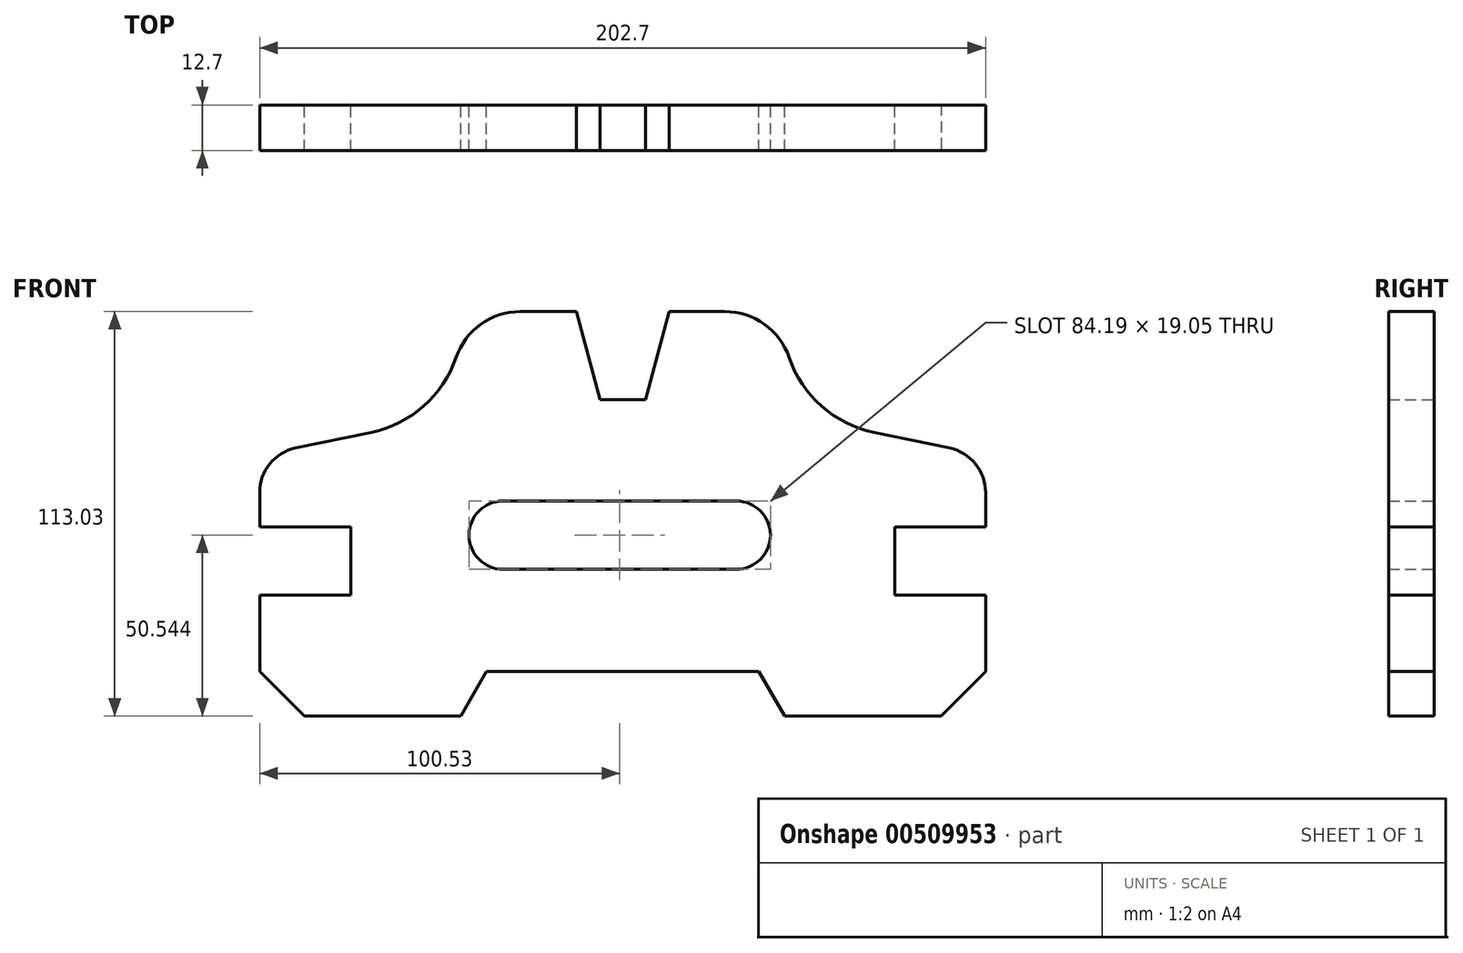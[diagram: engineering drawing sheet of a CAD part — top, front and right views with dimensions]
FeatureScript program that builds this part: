
annotation { "Feature Type Name" : "Feature", "Feature Type Description" : "" }
export const myFeature = defineFeature(function(context is Context, id is Id, definition is map)
    precondition{}
    {
        {
            var Q0;
            Q0=qCreatedBy(makeId("Front.planeOp"),FACE);
            var sketch = newSketch(context, id + "F0", { "sketchPlane" : qUnion([Q0])});
            skLineSegment(sketch, "E0", {"start": v(0, 75.85) * mm, "end": v(0, -76.26) * mm, "construction": true});
            skLineSegment(sketch, "E1", {"start": v(0, 38.24) * mm, "end": v(6.35, 38.24) * mm});
            skLineSegment(sketch, "E2", {"start": v(6.35, 38.24) * mm, "end": v(12.95, 62.88) * mm});
            skLineSegment(sketch, "E3", {"start": v(12.95, 62.88) * mm, "end": v(28.5, 62.88) * mm});
            skArc(sketch, "E4", {"start": v(28.5, 62.88) * mm, "mid": v(39.58, 59.32) * mm, "end": v(46.52, 49.98) * mm});
            skArc(sketch, "E5", {"start": v(46.52, 49.98) * mm, "mid": v(55.55, 36.45) * mm, "end": v(70.1, 29.16) * mm});
            skLineSegment(sketch, "E6", {"start": v(70.1, 29.16) * mm, "end": v(91.23, 24.77) * mm});
            skArc(sketch, "E7", {"start": v(91.23, 24.77) * mm, "mid": v(98.5, 20.35) * mm, "end": v(101.35, 12.33) * mm});
            skLineSegment(sketch, "E8", {"start": v(101.35, 12.33) * mm, "end": v(101.35, 2.68) * mm});
            skLineSegment(sketch, "E9", {"start": v(101.35, 2.68) * mm, "end": v(75.95, 2.68) * mm});
            skLineSegment(sketch, "E10", {"start": v(75.95, 2.68) * mm, "end": v(75.95, -16.37) * mm});
            skLineSegment(sketch, "E11", {"start": v(75.95, -16.37) * mm, "end": v(101.35, -16.37) * mm});
            skLineSegment(sketch, "E12", {"start": v(101.35, -16.37) * mm, "end": v(101.35, -50.15) * mm});
            skLineSegment(sketch, "E13", {"start": v(101.35, -50.15) * mm, "end": v(45.21, -50.15) * mm});
            skLineSegment(sketch, "E14", {"start": v(45.21, -50.15) * mm, "end": v(38.03, -37.7) * mm});
            skLineSegment(sketch, "E15", {"start": v(38.03, -37.7) * mm, "end": v(0, -37.7) * mm});
            skLineSegment(sketch, "E16.MirrorCS", {"start": v(0, 38.24) * mm, "end": v(-6.35, 38.24) * mm});
            skLineSegment(sketch, "E17.MirrorCS", {"start": v(-6.35, 38.24) * mm, "end": v(-12.95, 62.88) * mm});
            skLineSegment(sketch, "E18.MirrorCS", {"start": v(-12.95, 62.88) * mm, "end": v(-28.5, 62.88) * mm});
            skArc(sketch, "E19.MirrorCS", {"start": v(-28.5, 62.88) * mm, "mid": v(-39.58, 59.32) * mm, "end": v(-46.52, 49.98) * mm});
            skArc(sketch, "E20.MirrorCS", {"start": v(-46.52, 49.98) * mm, "mid": v(-55.55, 36.45) * mm, "end": v(-70.1, 29.16) * mm});
            skLineSegment(sketch, "E21.MirrorCS", {"start": v(-70.1, 29.16) * mm, "end": v(-91.23, 24.77) * mm});
            skArc(sketch, "E22.MirrorCS", {"start": v(-91.23, 24.77) * mm, "mid": v(-98.5, 20.35) * mm, "end": v(-101.35, 12.33) * mm});
            skLineSegment(sketch, "E23.MirrorCS", {"start": v(-101.35, 12.33) * mm, "end": v(-101.35, 2.68) * mm});
            skLineSegment(sketch, "E24.MirrorCS", {"start": v(-101.35, 2.68) * mm, "end": v(-75.95, 2.68) * mm});
            skLineSegment(sketch, "E25.MirrorCS", {"start": v(-75.95, 2.68) * mm, "end": v(-75.95, -16.37) * mm});
            skLineSegment(sketch, "E26.MirrorCS", {"start": v(-75.95, -16.37) * mm, "end": v(-101.35, -16.37) * mm});
            skLineSegment(sketch, "E27.MirrorCS", {"start": v(-101.35, -16.37) * mm, "end": v(-101.35, -50.15) * mm});
            skLineSegment(sketch, "E28.MirrorCS", {"start": v(-101.35, -50.15) * mm, "end": v(-45.21, -50.15) * mm});
            skLineSegment(sketch, "E29.MirrorCS", {"start": v(-45.21, -50.15) * mm, "end": v(-38.03, -37.7) * mm});
            skLineSegment(sketch, "E30.MirrorCS", {"start": v(-38.03, -37.7) * mm, "end": v(0, -37.7) * mm});
            skLineSegment(sketch, "E31", {"start": v(-33.39, 9.92) * mm, "end": v(31.75, 9.92) * mm});
            skLineSegment(sketch, "E32", {"start": v(-33.39, -9.13) * mm, "end": v(31.75, -9.13) * mm});
            skArc(sketch, "E33", {"start": v(31.75, 9.92) * mm, "mid": v(41.27, 0.4) * mm, "end": v(31.75, -9.13) * mm});
            skArc(sketch, "E34", {"start": v(-33.39, 9.92) * mm, "mid": v(-42.91, 0.4) * mm, "end": v(-33.39, -9.13) * mm});
            skLineSegment(sketch, "E35", {"start": v(-6.35, 38.24) * mm, "end": v(-6.35, 71.78) * mm, "construction": true});
            skLineSegment(sketch, "E36", {"start": v(6.35, 38.24) * mm, "end": v(6.35, 73.64) * mm, "construction": true});
            skLineSegment(sketch, "E37", {"start": v(-38.03, -37.7) * mm, "end": v(-38.03, -59.9) * mm, "construction": true});
            skLineSegment(sketch, "E38", {"start": v(38.03, -37.7) * mm, "end": v(38.03, -51.33) * mm, "construction": true});
            skSolve(sketch);
        }
        {
            var Q0;
            Q0 = qSketchRegion(id + "F0", true);
            extrude(context, id + "F1", {"entities" : qUnion([Q0]), "endBound" : BoundingType.SYMMETRIC, "depth" : 12.7 * mm, "offsetDistance" : 25.4 * mm});
        }
        {
            var Q0;
            Q0=makeQuery(id+"F1.opExtrude","SWEPT_EDGE",EDGE,{"disambiguationData":[OSD([sQuery(id+"F0.wireOp",EDGE,"E27.MirrorCS"),sQuery(id+"F0.wireOp",EDGE,"E28.MirrorCS")])]});
            var Q1;
            Q1=makeQuery(id+"F1.opExtrude","SWEPT_EDGE",EDGE,{"disambiguationData":[OSD([sQuery(id+"F0.wireOp",EDGE,"E12"),sQuery(id+"F0.wireOp",EDGE,"E13")])]});
            chamfer(context, id + "F2", {"entities" : qUnion([Q0, Q1]), "width" : 12.45 * mm, "tangentPropagation" : true});
        }
    });
